# Revit family: AFX-Glo-Led_Sconce-Vanity-1
name_source: partatom
category: Lighting Fixtures
units: mm (PartAtom-declared; Revit-internal decimal feet)

## family parameters
Cut with Voids When Loaded = No
Host = Face
Light Source = Yes
Part Type = Normal
Room Calculation Point = No
Round Connector Dimension = Use Diameter
Shared = No

## types (2) — shared parameters
Apparent Load = 120 VA
Assembly Code = D5020200
Body Finish = AFX - Aluminum Black
Cable Finish = AFX - Aluminum Black
Canopy Finish = AFX - Aluminum Black
Color Filter = 16777215
Color Rendering Index = 90
Colour Rendering Index = 90 CRI
Connector Finish = AFX - Aluminum Black
Default Elevation = 48"
Depth = 2 1/2"
Diffuser Finish = AFX - White Acrylic
Dimming Lamp Color Temperature Shift = <None>
Emit Shape Visible in Rendering = No
Emit from Rectangle Length = 48"
Emit from Rectangle Width = 24"
Lamp = LED
Manufacturer = AFX Inc
Product Documentation Link = https://www.afxinc.com
Revit Model Built By = https://servex-us.com
Tilt Angle = 90.00°
Type Comments = GLO
URL = https://www.afxinc.com
Voltage = 120 V
Wattage Comments = 12W
Width = 4 3/4"

## per-type parameters (varying)
| type | Description | Height | Photometric Web File | Qty L |
| GLOS0514L30D1BK | LED Sconce - 14 1/4"H x 4 3/4"W x 2 1/2"D | 14 1/4" | GLOS0514L30D1xx_IES.IES | 3 |
| GLOV2405L30D1BK | LED Vanity - 24"H x 4 3/4"W x 2 1/2"D | 24" | GLOV2405L30D1xx_IES.IES | 5 |

note: column(s) folded — value = type name in every type: Model

## geometry (parser evidence)
native form markers: Sweep x3
no freeform markers — native parametric forms only
